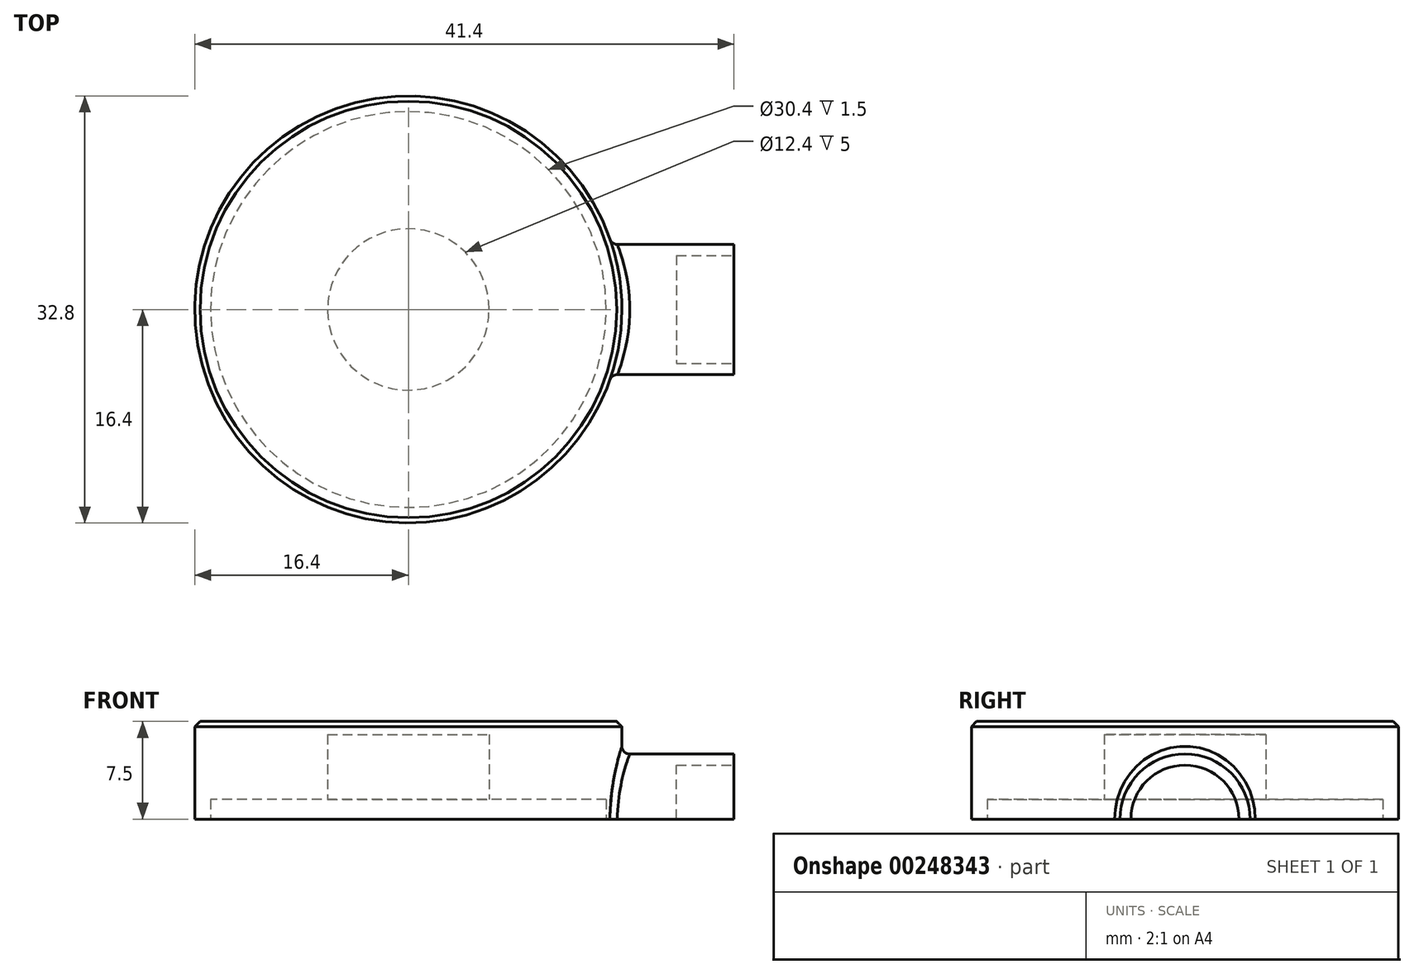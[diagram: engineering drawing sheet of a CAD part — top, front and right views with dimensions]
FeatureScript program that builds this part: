
annotation { "Feature Type Name" : "Feature", "Feature Type Description" : "" }
export const myFeature = defineFeature(function(context is Context, id is Id, definition is map)
    precondition{}
    {
        {
            var Q0;
            Q0=qCreatedBy(makeId("Top.planeOp"),FACE);
            var sketch = newSketch(context, id + "F0", { "sketchPlane" : qUnion([Q0])});
            skCircle(sketch, "E0", {"center": v(0, 0) * mm, "radius": 16.4 * mm});
            skSolve(sketch);
        }
        {
            var Q0;
            Q0=qSketchRegion(id+"F0",true);
            extrude(context, id + "F1", {"entities" : qUnion([Q0]), "depth" : 15 * mm});
        }
        {
            var Q0;
            Q0=makeQuery(id+"F1.opExtrude","CAP_FACE",FACE,{"disambiguationData":[OSD([sQuery(id+"F0.wireOp",EDGE,"E0")])],"isStart":true});
            var sketch = newSketch(context, id + "F2", { "sketchPlane" : qUnion([Q0])});
            skCircle(sketch, "E1", {"center": v(0, 0) * mm, "radius": 15.2 * mm});
            skSolve(sketch);
        }
        {
            var Q0;
            Q0=qSketchRegion(id+"F2",true);
            extrude(context, id + "F3", {"entities" : qUnion([Q0]), "operationType" : NewBodyOperationType.REMOVE, "oppositeDirection" : true, "depth" : 2 * mm});
        }
        {
            var Q0;
            Q0=makeQuery(id+"F3.boolean.opBoolean","COPY",FACE,{"derivedFrom":makeQuery(id+"F3.opExtrude","CAP_FACE",FACE,{"disambiguationData":[OSD([sQuery(id+"F2.wireOp",EDGE,"E1")])],"isStart":false})});
            var sketch = newSketch(context, id + "F4", { "sketchPlane" : qUnion([Q0])});
            skCircle(sketch, "E2", {"center": v(0, 0) * mm, "radius": 11 * mm});
            skSolve(sketch);
        }
        {
            var Q0;
            Q0=qSketchRegion(id+"F4",true);
            extrude(context, id + "F5", {"entities" : qUnion([Q0]), "operationType" : NewBodyOperationType.REMOVE, "oppositeDirection" : true, "depth" : 25 * mm});
        }
        {
            var Q0;
            Q0=makeQuery(id+"F1.opExtrude","CAP_FACE",FACE,{"disambiguationData":[OSD([sQuery(id+"F0.wireOp",EDGE,"E0")])],"isStart":false});
            var sketch = newSketch(context, id + "F6", { "sketchPlane" : qUnion([Q0])});
            skCircle(sketch, "E3", {"center": v(0, 0) * mm, "radius": 15.2 * mm});
            skSolve(sketch);
        }
        {
            var Q0;
            Q0=qSketchRegion(id+"F6",true);
            extrude(context, id + "F7", {"entities" : qUnion([Q0]), "operationType" : NewBodyOperationType.REMOVE, "oppositeDirection" : true, "depth" : 10.4 * mm});
        }
        {
            var Q0;
            Q0=makeQuery(id+"F1.opExtrude","CAP_FACE",FACE,{"disambiguationData":[OSD([sQuery(id+"F0.wireOp",EDGE,"E0")])],"isStart":false});
            var sketch = newSketch(context, id + "F8", { "sketchPlane" : qUnion([Q0])});
            skCircle(sketch, "E4", {"center": v(0, 0) * mm, "radius": 15.5 * mm});
            skSolve(sketch);
        }
        {
            var Q0;
            Q0=qSketchRegion(id+"F8",true);
            extrude(context, id + "F9", {"entities" : qUnion([Q0]), "operationType" : NewBodyOperationType.ADD, "oppositeDirection" : true, "depth" : 6 * mm});
        }
        {
            var Q0;
            Q0=makeQuery(id+"F9.opExtrude","CAP_FACE",FACE,{"disambiguationData":[OSD([sQuery(id+"F8.wireOp",EDGE,"E4")])],"isStart":false});
            var sketch = newSketch(context, id + "F10", { "sketchPlane" : qUnion([Q0])});
            skCircle(sketch, "E5", {"center": v(0, 0) * mm, "radius": 6.2 * mm});
            skSolve(sketch);
        }
        {
            var Q0;
            Q0=qSketchRegion(id+"F10",true);
            extrude(context, id + "F11", {"entities" : qUnion([Q0]), "operationType" : NewBodyOperationType.REMOVE, "oppositeDirection" : true, "depth" : 5 * mm});
        }
        {
            var Q0;
            Q0=makeQuery(id+"F3.boolean.opBoolean","COPY",FACE,{"derivedFrom":makeQuery(id+"F3.opExtrude","CAP_FACE",FACE,{"disambiguationData":[OSD([sQuery(id+"F2.wireOp",EDGE,"E1")])],"isStart":false})});
            var sketch = newSketch(context, id + "F12", { "sketchPlane" : qUnion([Q0])});
            skLineSegment(sketch, "E6.bottom", {"start": v(1.5, 18) * mm, "end": v(-1.5, 18) * mm});
            skLineSegment(sketch, "E6.top", {"start": v(1.5, -18) * mm, "end": v(-1.5, -18) * mm});
            skLineSegment(sketch, "E6.left", {"start": v(1.5, 18) * mm, "end": v(1.5, -18) * mm});
            skLineSegment(sketch, "E6.right", {"start": v(-1.5, 18) * mm, "end": v(-1.5, -18) * mm});
            skPoint(sketch, "E6.middle", {"position": v(0, 0) * mm});
            skCircle(sketch, "E7.0", {"center": v(0, 0) * mm, "radius": 15.2 * mm});
            skSolve(sketch);
        }
        {
            var Q0;
            {var subQ0=sQuery(id+"F12.wireOp",EDGE,"E7.0");var subQ1=sQuery(id+"F12.wireOp",EDGE,"E6.left");var subQ2=makeQuery(id+"F12.imprint","INTERSECT",VERTEX,{"disambiguationData":[OD(0.0)],"derivedFrom":[subQ1,subQ0]});Q0=makeQuery(id+"F12.imprint","IMPRINT",FACE,{"disambiguationData":[TD([[makeQuery(id+"F12.imprint","IMPRINT",EDGE,{"disambiguationData":[TD([[subQ2,-1.0]])],"derivedFrom":subQ1}),-1.0]])]});}
            var Q1;
            {var subQ0=sQuery(id+"F12.wireOp",EDGE,"E7.0");var subQ1=sQuery(id+"F12.wireOp",EDGE,"E6.left");var subQ2=makeQuery(id+"F12.imprint","INTERSECT",VERTEX,{"disambiguationData":[OD(1.0)],"derivedFrom":[subQ1,subQ0]});Q1=makeQuery(id+"F12.imprint","IMPRINT",FACE,{"disambiguationData":[TD([[makeQuery(id+"F12.imprint","IMPRINT",EDGE,{"disambiguationData":[TD([[subQ2,1.0]])],"derivedFrom":subQ1}),-1.0]])]});}
            extrude(context, id + "F13", {"entities" : qUnion([Q0, Q1]), "operationType" : NewBodyOperationType.REMOVE, "oppositeDirection" : true, "depth" : 5 * mm});
        }
        {
            var Q0;
            Q0=qCreatedBy(makeId("Right.planeOp"),FACE);
            var sketch = newSketch(context, id + "F14", { "sketchPlane" : qUnion([Q0])});
            skCircle(sketch, "E8", {"center": v(0, 7.5) * mm, "radius": 5 * mm});
            skSolve(sketch);
        }
        {
            var Q0;
            Q0=qSketchRegion(id+"F14",true);
            var Q1;
            Q1=makeQuery(id+"F1.opExtrude","SWEPT_BODY",BODY,{"disambiguationData":[OSD([sQuery(id+"F0.wireOp",EDGE,"E0")])]});
            extrude(context, id + "F15", {"entities" : qUnion([Q0]), "operationType" : NewBodyOperationType.ADD, "depth" : 25 * mm, "hasSecondDirection" : true, "secondDirectionBound" : SecondDirectionBoundingType.UP_TO_BODY, "secondDirectionOppositeDirection" : false, "secondDirectionBoundEntityBody" : qUnion([Q1]), "secondDirectionDepth" : 25 * mm});
        }
        {
            var Q0;
            Q0=makeQuery(id+"F15.boolean.opBoolean","INTERSECT",EDGE,{"derivedFrom":[makeQuery(id+"F1.opExtrude","SWEPT_FACE",FACE,{"disambiguationData":[OSD([sQuery(id+"F0.wireOp",EDGE,"E0")])]}),makeQuery(id+"F15.opExtrude","SWEPT_FACE",FACE,{"disambiguationData":[OSD([sQuery(id+"F14.wireOp",EDGE,"E8")])]})]});
            fillet(context, id + "F16", {"entities" : qUnion([Q0]), "radius" : 0.6 * mm, "tangentPropagation" : true, "allowEdgeOverflow" : false});
        }
        {
            var Q0;
            Q0=makeQuery(id+"F1.opExtrude","CAP_EDGE",EDGE,{"disambiguationData":[OSD([sQuery(id+"F0.wireOp",EDGE,"E0")])],"isStart":true});
            var Q1;
            Q1=makeQuery(id+"F1.opExtrude","CAP_EDGE",EDGE,{"disambiguationData":[OSD([sQuery(id+"F0.wireOp",EDGE,"E0")])],"isStart":false});
            chamfer(context, id + "F17", {"entities" : qUnion([Q0, Q1]), "width" : 0.4 * mm, "tangentPropagation" : true});
        }
        {
            var Q0;
            Q0=makeQuery(id+"F15.opExtrude","CAP_FACE",FACE,{"disambiguationData":[OSD([sQuery(id+"F14.wireOp",EDGE,"E8")])],"isStart":false});
            var sketch = newSketch(context, id + "F18", { "sketchPlane" : qUnion([Q0])});
            skCircle(sketch, "E9", {"center": v(0, 7.5) * mm, "radius": 4.15 * mm});
            skSolve(sketch);
        }
        {
            var Q0;
            Q0=qSketchRegion(id+"F18",true);
            extrude(context, id + "F19", {"entities" : qUnion([Q0]), "operationType" : NewBodyOperationType.REMOVE, "oppositeDirection" : true, "depth" : 4.4 * mm});
        }
        {
            var Q0;
            Q0=qCreatedBy(makeId("Top.planeOp"),FACE);
            cPlane(context, id + "F20", {"entities" : qUnion([Q0]), "cplaneType" : CPlaneType.OFFSET, "offset" : 7.5 * mm, "width" : 150 * mm, "height" : 150 * mm});
        }
        {
            var Q0;
            Q0=qCreatedBy(id+"F20.planeOp",FACE);
            var sketch = newSketch(context, id + "F21", { "sketchPlane" : qUnion([Q0])});
            skCircle(sketch, "E10", {"center": v(0, 0) * mm, "radius": 45.33 * mm});
            skSolve(sketch);
        }
        {
            var Q0;
            Q0 = qSketchRegion(id + "F21", true);
            extrude(context, id + "F22", {"entities" : qUnion([Q0]), "operationType" : NewBodyOperationType.REMOVE, "oppositeDirection" : true, "depth" : 25 * mm});
        }
    });
